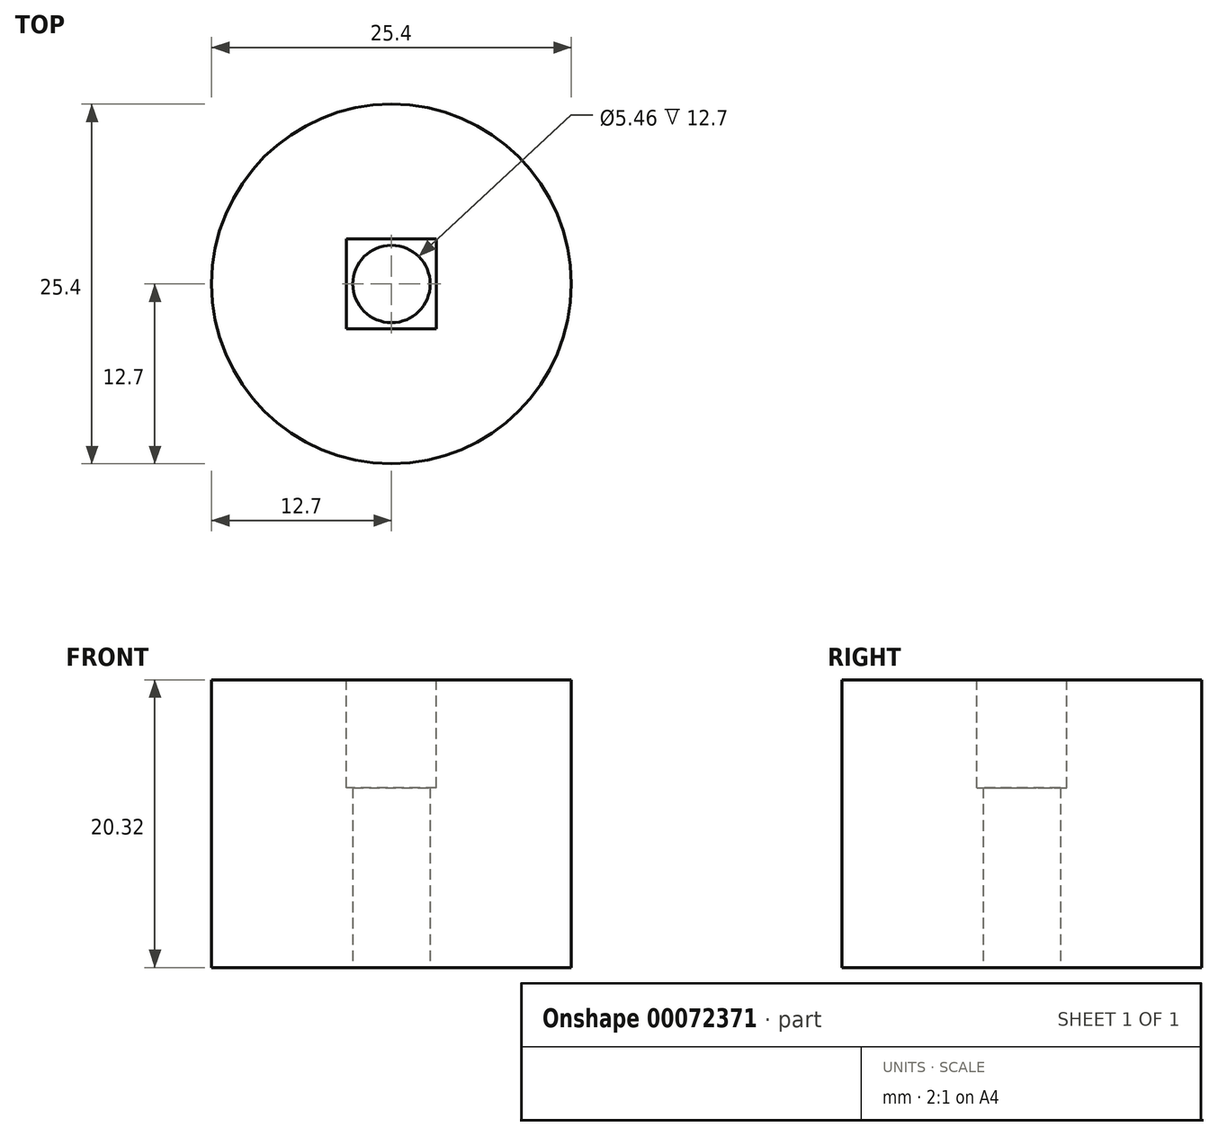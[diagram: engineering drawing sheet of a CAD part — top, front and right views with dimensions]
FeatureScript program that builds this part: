
annotation { "Feature Type Name" : "Feature", "Feature Type Description" : "" }
export const myFeature = defineFeature(function(context is Context, id is Id, definition is map)
    precondition{}
    {
        {
            var Q0;
            Q0=qCreatedBy(makeId("Top.planeOp"),FACE);
            var sketch = newSketch(context, id + "F0", { "sketchPlane" : qUnion([Q0])});
            skCircle(sketch, "E0", {"center": v(0, 0) * mm, "radius": 12.7 * mm});
            skSolve(sketch);
        }
        {
            var Q0;
            Q0 = qSketchRegion(id + "F0", true);
            extrude(context, id + "F1", {"entities" : qUnion([Q0]), "endBound" : BoundingType.SYMMETRIC, "depth" : 20.32 * mm});
        }
        {
            var Q0;
            Q0=makeQuery(id+"F1.opExtrude","CAP_FACE",FACE,{"disambiguationData":[OSD([sQuery(id+"F0.wireOp",EDGE,"E0")])],"isStart":false});
            var sketch = newSketch(context, id + "F2", { "sketchPlane" : qUnion([Q0])});
            skLineSegment(sketch, "E1.bottom", {"start": v(0, 0) * mm, "end": v(3.17, 0) * mm});
            skLineSegment(sketch, "E1.top", {"start": v(0, 3.17) * mm, "end": v(3.17, 3.17) * mm});
            skLineSegment(sketch, "E1.left", {"start": v(0, 0) * mm, "end": v(0, 3.17) * mm});
            skLineSegment(sketch, "E1.right", {"start": v(3.17, 0) * mm, "end": v(3.17, 3.17) * mm});
            skLineSegment(sketch, "E2.bottom", {"start": v(0, 0) * mm, "end": v(-3.18, 0) * mm});
            skLineSegment(sketch, "E2.top", {"start": v(0, 3.18) * mm, "end": v(-3.18, 3.17) * mm});
            skLineSegment(sketch, "E2.right", {"start": v(-3.18, 0) * mm, "end": v(-3.18, 3.17) * mm});
            skLineSegment(sketch, "E3.top", {"start": v(0, -3.18) * mm, "end": v(-3.18, -3.17) * mm});
            skLineSegment(sketch, "E3.left", {"start": v(0, 0) * mm, "end": v(0, -3.17) * mm});
            skLineSegment(sketch, "E3.right", {"start": v(-3.18, 0) * mm, "end": v(-3.18, -3.17) * mm});
            skLineSegment(sketch, "E4.top", {"start": v(0, -3.18) * mm, "end": v(3.17, -3.18) * mm});
            skLineSegment(sketch, "E4.right", {"start": v(3.17, 0) * mm, "end": v(3.17, -3.18) * mm});
            skLineSegment(sketch, "E5.bottom", {"start": v(-3.18, 3.18) * mm, "end": v(3.17, 3.17) * mm});
            skLineSegment(sketch, "E5.top", {"start": v(-3.18, -3.18) * mm, "end": v(3.17, -3.18) * mm});
            skLineSegment(sketch, "E5.left", {"start": v(-3.17, 3.18) * mm, "end": v(-3.18, -3.17) * mm});
            skLineSegment(sketch, "E5.right", {"start": v(3.17, 3.17) * mm, "end": v(3.17, -3.18) * mm});
            skSolve(sketch);
        }
        {
            var Q0;
            {var subQ0=sQuery(id+"F2.wireOp",EDGE,"E1.left");Q0=makeQuery(id+"F2.imprint","IMPRINT",FACE,{"disambiguationData":[TD([[makeQuery(id+"F2.imprint","IMPRINT",EDGE,{"derivedFrom":subQ0}),1.0]])]});}
            var Q1;
            {var subQ0=sQuery(id+"F2.wireOp",EDGE,"E1.left");Q1=makeQuery(id+"F2.imprint","IMPRINT",FACE,{"disambiguationData":[TD([[makeQuery(id+"F2.imprint","IMPRINT",EDGE,{"derivedFrom":subQ0}),-1.0]])]});}
            var Q2;
            {var subQ0=sQuery(id+"F2.wireOp",EDGE,"E2.bottom");Q2=makeQuery(id+"F2.imprint","IMPRINT",FACE,{"disambiguationData":[TD([[makeQuery(id+"F2.imprint","IMPRINT",EDGE,{"derivedFrom":subQ0}),1.0]])]});}
            var Q3;
            {var subQ0=sQuery(id+"F2.wireOp",EDGE,"E1.bottom");Q3=makeQuery(id+"F2.imprint","IMPRINT",FACE,{"disambiguationData":[TD([[makeQuery(id+"F2.imprint","IMPRINT",EDGE,{"derivedFrom":subQ0}),-1.0]])]});}
            extrude(context, id + "F3", {"entities" : qUnion([Q0, Q1, Q2, Q3]), "operationType" : NewBodyOperationType.REMOVE, "endBound" : BoundingType.SYMMETRIC, "oppositeDirection" : true, "depth" : 15.24 * mm});
        }
        {
            var Q0;
            Q0=makeQuery(id+"F1.opExtrude","CAP_FACE",FACE,{"disambiguationData":[OSD([sQuery(id+"F0.wireOp",EDGE,"E0")])],"isStart":true});
            var sketch = newSketch(context, id + "F4", { "sketchPlane" : qUnion([Q0])});
            skCircle(sketch, "E6", {"center": v(0, 0) * mm, "radius": 2.73 * mm});
            skSolve(sketch);
        }
        {
            var Q0;
            Q0 = qSketchRegion(id + "F4", true);
            extrude(context, id + "F5", {"entities" : qUnion([Q0]), "operationType" : NewBodyOperationType.REMOVE, "endBound" : BoundingType.SYMMETRIC, "oppositeDirection" : true, "depth" : 25.4 * mm});
        }
    });
